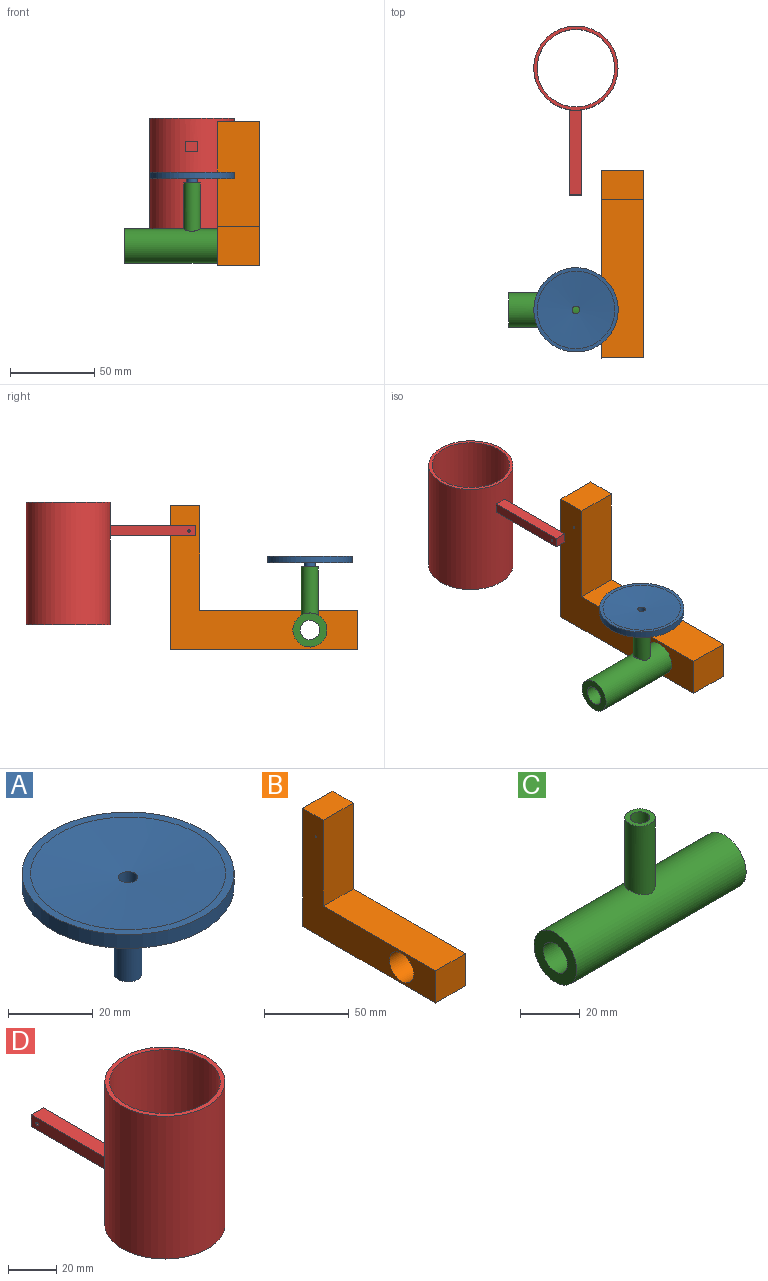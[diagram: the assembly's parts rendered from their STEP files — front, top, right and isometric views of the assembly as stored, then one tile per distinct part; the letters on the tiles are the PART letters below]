
ASSEMBLY  parts=4 mates=3
PART A: 7 faces, bbox 50x50x29 mm
  f0: cone r=23mm half-angle=86.9deg, axis (0,0,1), area 1648.1mm2, adj f1,f4
  f1: plane 50x50mm, normal (0,0,1), area 301.6mm2, adj f0,f2
  f2: cylinder r=25mm len=50mm, axis (0,0,1), area 629.6mm2, adj f1,f3
  f3: plane 50x50mm, normal (0,0,-1), area 1929.6mm2, adj f2,f5
  f4: cylinder r=2.27mm len=27.88mm, axis (0,0,-1), area 398.4mm2, adj f0,f6
  f5: cylinder r=3.29mm len=25mm, axis (0,0,1), area 516.2mm2, adj f3,f6
  f6: plane 6.57x6.57mm, normal (0,0,-1), area 17.7mm2, adj f4,f5
PART B: 10 faces, bbox 25x111.2x85.5 mm
  f0: plane 62.24x25mm, normal (0,-1,0), area 1555.9mm2, adj f1,f5,f8,f9
  f1: plane 93.83x25mm, normal (0,0,1), area 2345.7mm2, adj f0,f2,f8,f9
  f2: plane 25x23.26mm, normal (0,-1,0), area 581.4mm2, adj f1,f3,f8,f9
  f3: plane 111.25x25mm, normal (0,0,-1), area 2781.2mm2, adj f2,f4,f8,f9
  f4: plane 85.49x25mm, normal (0,1,0), area 2137.4mm2, adj f3,f5,f8,f9
  f5: plane 25x17.42mm, normal (0,0,1), area 435.5mm2, adj f0,f4,f8,f9
  f6: cylinder r=0.66mm len=25mm, axis (-1,0,0), area 103.9mm2, adj f8,f9
  f7: cylinder r=10.09mm len=25mm, axis (-1,0,0), area 1585.6mm2, adj f8,f9
  f8: plane 111.25x85.49mm, normal (1,0,0), area 3350mm2, adj f0,f1,f2,f3,f4,f5,f6,f7
  f9: plane 111.25x85.49mm, normal (-1,0,0), area 3350mm2, adj f0,f1,f2,f3,f4,f5,f6,f7
PART C: 8 faces, bbox 80x20.2x47.4 mm
  f0: cylinder r=3.29mm len=27.81mm, axis (0,0,1), area 568.5mm2, adj f2,f7
  f1: cylinder r=5.04mm len=28.61mm, axis (0,0,1), area 883.7mm2, adj f2,f6
  f2: plane 10.08x10.08mm, normal (0,0,1), area 45.8mm2, adj f0,f1
  f3: plane 20.19x20.19mm, normal (-1,0,0), area 217.3mm2, adj f5,f6
  f4: plane 20.19x20.19mm, normal (1,0,0), area 217.3mm2, adj f5,f6
  f5: cylinder r=5.72mm len=80mm, axis (-1,0,0), area 2874.8mm2, adj f3,f4
  f6: cylinder r=10.09mm len=80mm, axis (-1,0,0), area 4991.5mm2, adj f1,f3,f4
  f7: cylinder r=10.09mm len=6.57mm, axis (-1,0,0), area 34.4mm2, adj f0
PART D: 10 faces, bbox 50x100.2x72.6 mm
  f0: cylinder r=25mm len=72.64mm, axis (0,0,1), area 11367.6mm2, adj f1,f3,f4,f5,f7,f8
  f1: plane 50x50mm, normal (0,0,-1), area 301.6mm2, adj f0,f2
  f2: cylinder r=23mm len=72.64mm, axis (0,0,1), area 10497.9mm2, adj f1,f3
  f3: plane 50x50mm, normal (0,0,1), area 301.6mm2, adj f0,f2
  f4: plane 50.43x6mm, normal (1,0,0), area 301.2mm2, adj f0,f6,f7,f8,f9
  f5: plane 50.43x6mm, normal (-1,0,0), area 301.2mm2, adj f0,f6,f7,f8,f9
  f6: plane 7.16x6mm, normal (0,1,0), area 42.9mm2, adj f4,f5,f7,f8
  f7: plane 50.43x7.16mm, normal (0,0,-1), area 359.7mm2, adj f0,f4,f5,f6
  f8: plane 50.43x7.16mm, normal (0,0,1), area 359.7mm2, adj f0,f4,f5,f6
  f9: cylinder r=0.66mm len=7.16mm, axis (-1,0,0), area 29.7mm2, adj f4,f5
PLACE A rot(axis=(0,0,-1),171deg) t=(-187.31,-16,46.23)mm
PLACE B t=(58.23,1.11,43.73)mm
PLACE C t=(30.73,1.11,43.73)mm fixed
PLACE D rot(axis=(1,0,0),180deg) t=(30.65,144.36,1.07)mm
MATE cylindrical A.f5 <-> C.f0  axis (0,0,1) through (-78.96,1.11,-8.9)mm
MATE fastened B.f7 <-> C.f5  axis (1,0,0) through (-38.96,1.11,-36.25)mm
MATE revolute B.f6 <-> D.f9  axis (-1,0,0) through (-63.96,72.74,22.4)mm
